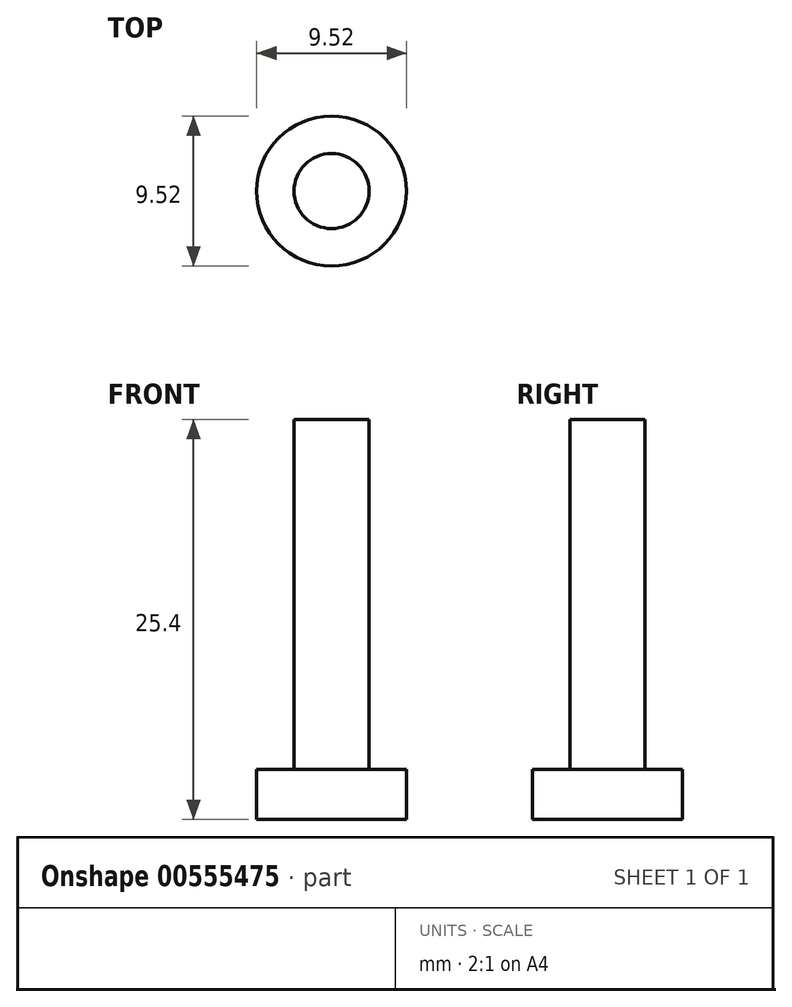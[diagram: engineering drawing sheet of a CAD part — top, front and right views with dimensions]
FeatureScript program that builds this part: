
annotation { "Feature Type Name" : "Feature", "Feature Type Description" : "" }
export const myFeature = defineFeature(function(context is Context, id is Id, definition is map)
    precondition{}
    {
        {
            var Q0;
            Q0=qCreatedBy(makeId("Top.planeOp"),FACE);
            var sketch = newSketch(context, id + "F0", { "sketchPlane" : qUnion([Q0])});
            skCircle(sketch, "E0", {"center": v(0, 0) * mm, "radius": 4.76 * mm});
            skCircle(sketch, "E1", {"center": v(0, 0) * mm, "radius": 2.38 * mm});
            skSolve(sketch);
        }
        {
            var Q0;
            Q0 = qSketchRegion(id + "F0", true);
            var Q1;
            Q1=makeQuery(id+"F0.imprint","IMPRINT",FACE,{"disambiguationData":[TD([[makeQuery(id+"F0.imprint","IMPRINT",EDGE,{"derivedFrom":sQuery(id+"F0.wireOp",EDGE,"E1")}),1.0]])]});
            extrude(context, id + "F1", {"entities" : qUnion([Q0, Q1]), "depth" : 3.17 * mm, "offsetDistance" : 25.4 * mm});
        }
        {
            var Q0;
            Q0=makeQuery(id+"F0.imprint","IMPRINT",FACE,{"disambiguationData":[TD([[makeQuery(id+"F0.imprint","IMPRINT",EDGE,{"derivedFrom":sQuery(id+"F0.wireOp",EDGE,"E1")}),1.0]])]});
            var Q1;
            Q1=sQuery(id+"F0.wireOp",EDGE,"E1");
            extrude(context, id + "F2", {"entities" : qUnion([Q0]), "operationType" : NewBodyOperationType.ADD, "surfaceEntities" : qUnion([Q1]), "depth" : 25.4 * mm, "offsetDistance" : 25.4 * mm});
        }
    });
